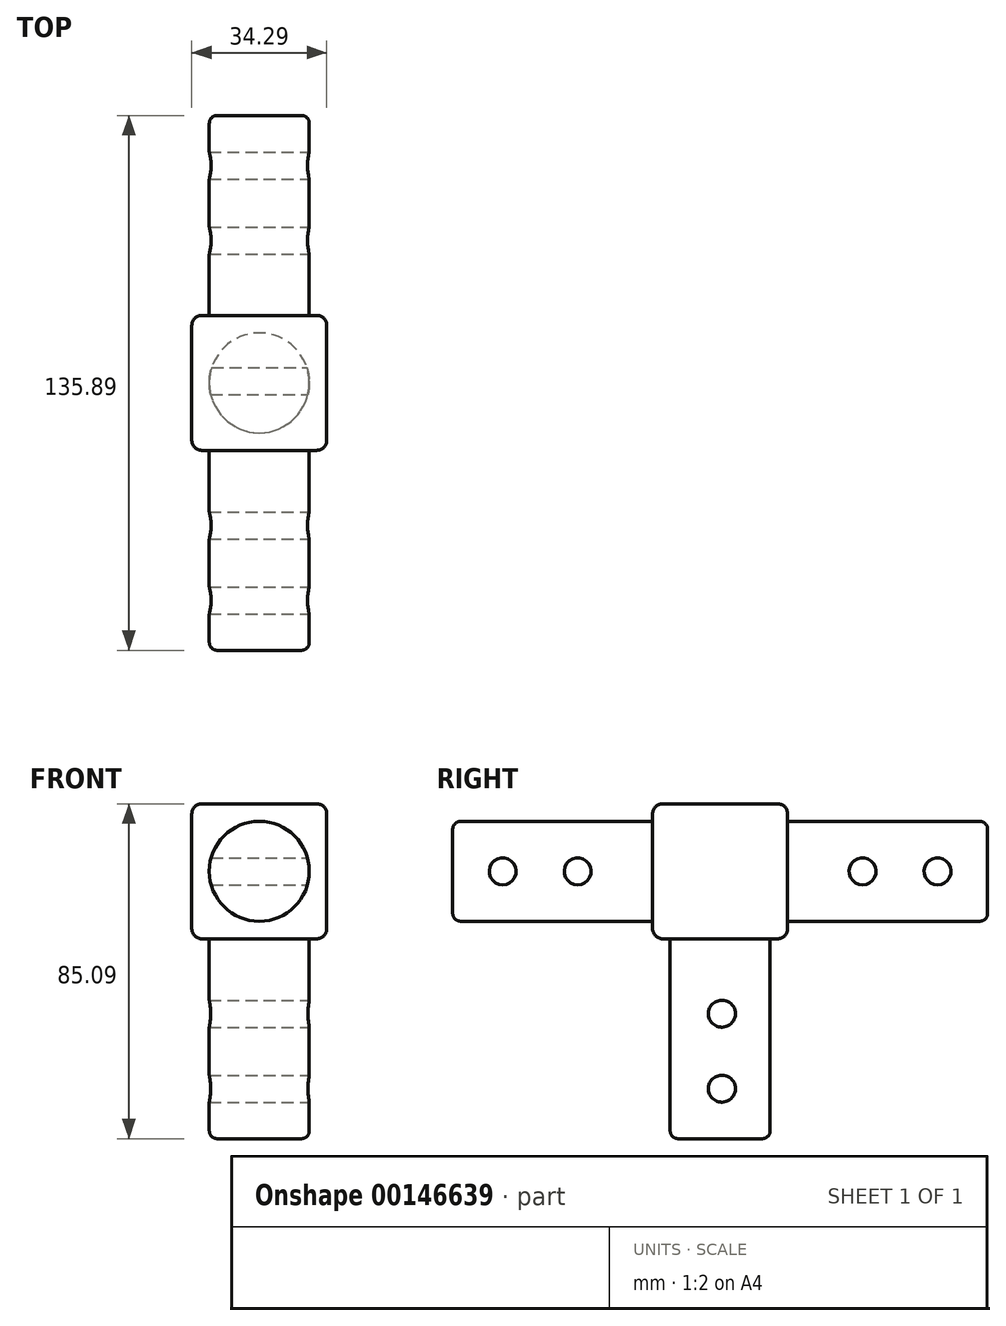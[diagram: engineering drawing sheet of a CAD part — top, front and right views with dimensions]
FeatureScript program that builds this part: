
annotation { "Feature Type Name" : "Feature", "Feature Type Description" : "" }
export const myFeature = defineFeature(function(context is Context, id is Id, definition is map)
    precondition{}
    {
        {
            var Q0;
            Q0=qCreatedBy(makeId("Top.planeOp"),FACE);
            var sketch = newSketch(context, id + "F0", { "sketchPlane" : qUnion([Q0])});
            skLineSegment(sketch, "E0.bottom", {"start": v(-13.47, 23.7) * mm, "end": v(20.82, 23.7) * mm});
            skLineSegment(sketch, "E0.top", {"start": v(-13.47, -10.58) * mm, "end": v(20.82, -10.58) * mm});
            skLineSegment(sketch, "E0.left", {"start": v(-13.47, 23.7) * mm, "end": v(-13.47, -10.58) * mm});
            skLineSegment(sketch, "E0.right", {"start": v(20.82, 23.7) * mm, "end": v(20.82, -10.58) * mm});
            skSolve(sketch);
        }
        {
            var Q0;
            Q0=qSketchRegion(id+"F0",true);
            extrude(context, id + "F1", {"entities" : qUnion([Q0]), "depth" : 34.3 * mm});
        }
        {
            var Q0;
            Q0=makeQuery(id+"F1.opExtrude","SWEPT_FACE",FACE,{"disambiguationData":[OSD([sQuery(id+"F0.wireOp",EDGE,"E0.top")])]});
            var sketch = newSketch(context, id + "F2", { "sketchPlane" : qUnion([Q0])});
            skLineSegment(sketch, "E1", {"start": v(-13.47, 17.15) * mm, "end": v(24.43, 17.15) * mm, "construction": true});
            skLineSegment(sketch, "E2", {"start": v(3.67, 0) * mm, "end": v(3.67, 34.3) * mm, "construction": true});
            skCircle(sketch, "E3", {"center": v(3.67, 17.15) * mm, "radius": 12.7 * mm});
            skSolve(sketch);
        }
        {
            var Q0;
            Q0=qSketchRegion(id+"F2",true);
            extrude(context, id + "F3", {"entities" : qUnion([Q0]), "operationType" : NewBodyOperationType.ADD, "depth" : 50.8 * mm});
        }
        {
            var Q0;
            Q0=qCreatedBy(makeId("Front.planeOp"),FACE);
            var sketch = newSketch(context, id + "F4", { "sketchPlane" : qUnion([Q0])});
            skCircle(sketch, "E4", {"center": v(3.67, 53.34) * mm, "radius": 3.43 * mm});
            skCircle(sketch, "E5", {"center": v(3.67, 72.4) * mm, "radius": 3.43 * mm});
            skSolve(sketch);
        }
        {
            var Q0;
            Q0=qSketchRegion(id+"F4",true);
            extrude(context, id + "F5", {"entities" : qUnion([Q0]), "operationType" : NewBodyOperationType.REMOVE, "endBound" : BoundingType.SYMMETRIC, "oppositeDirection" : true, "depth" : 50.8 * mm});
        }
        {
            var Q0;
            Q0=qCreatedBy(makeId("Right.planeOp"),FACE);
            var sketch = newSketch(context, id + "F6", { "sketchPlane" : qUnion([Q0])});
            skCircle(sketch, "E6", {"center": v(-29.63, 17.15) * mm, "radius": 3.43 * mm});
            skCircle(sketch, "E7", {"center": v(-48.68, 17.15) * mm, "radius": 3.43 * mm});
            skSolve(sketch);
        }
        {
            var Q0;
            Q0=qSketchRegion(id+"F6",true);
            extrude(context, id + "F7", {"entities" : qUnion([Q0]), "operationType" : NewBodyOperationType.REMOVE, "endBound" : BoundingType.SYMMETRIC, "oppositeDirection" : true, "depth" : 50.8 * mm});
        }
        {
            var Q0;
            Q0=qCreatedBy(makeId("Front.planeOp"),FACE);
            var sketch = newSketch(context, id + "F8", { "sketchPlane" : qUnion([Q0])});
            skCircle(sketch, "E8", {"center": v(-51.57, 17.15) * mm, "radius": 3.43 * mm});
            skCircle(sketch, "E9", {"center": v(-32.52, 17.15) * mm, "radius": 3.43 * mm});
            skSolve(sketch);
        }
        {
            var Q0;
            Q0=qSketchRegion(id+"F8",true);
            extrude(context, id + "F9", {"entities" : qUnion([Q0]), "operationType" : NewBodyOperationType.REMOVE, "endBound" : BoundingType.SYMMETRIC, "oppositeDirection" : true, "depth" : 50.8 * mm});
        }
        {
            var Q0;
            Q0=makeQuery(id+"F1.opExtrude","SWEPT_EDGE",EDGE,{"disambiguationData":[OSD([sQuery(id+"F0.wireOp",EDGE,"E0.bottom"),sQuery(id+"F0.wireOp",EDGE,"E0.right")])]});
            var Q1;
            Q1=makeQuery(id+"F1.opExtrude","CAP_EDGE",EDGE,{"disambiguationData":[OSD([sQuery(id+"F0.wireOp",EDGE,"E0.right")])],"isStart":false});
            var Q2;
            Q2=makeQuery(id+"F1.opExtrude","SWEPT_EDGE",EDGE,{"disambiguationData":[OSD([sQuery(id+"F0.wireOp",EDGE,"E0.top"),sQuery(id+"F0.wireOp",EDGE,"E0.right")])]});
            var Q3;
            Q3=makeQuery(id+"F1.opExtrude","CAP_EDGE",EDGE,{"disambiguationData":[OSD([sQuery(id+"F0.wireOp",EDGE,"E0.right")])],"isStart":true});
            var Q4;
            Q4=makeQuery(id+"F1.opExtrude","CAP_EDGE",EDGE,{"disambiguationData":[OSD([sQuery(id+"F0.wireOp",EDGE,"E0.bottom")])],"isStart":true});
            var Q5;
            Q5=makeQuery(id+"F1.opExtrude","CAP_EDGE",EDGE,{"disambiguationData":[OSD([sQuery(id+"F0.wireOp",EDGE,"E0.bottom")])],"isStart":false});
            var Q6;
            Q6=makeQuery(id+"F1.opExtrude","SWEPT_EDGE",EDGE,{"disambiguationData":[OSD([sQuery(id+"F0.wireOp",EDGE,"E0.bottom"),sQuery(id+"F0.wireOp",EDGE,"E0.left")])]});
            var Q7;
            Q7=makeQuery(id+"F1.opExtrude","CAP_EDGE",EDGE,{"disambiguationData":[OSD([sQuery(id+"F0.wireOp",EDGE,"E0.left")])],"isStart":true});
            var Q8;
            Q8=makeQuery(id+"F1.opExtrude","CAP_EDGE",EDGE,{"disambiguationData":[OSD([sQuery(id+"F0.wireOp",EDGE,"E0.top")])],"isStart":true});
            var Q9;
            Q9=makeQuery(id+"F1.opExtrude","CAP_EDGE",EDGE,{"disambiguationData":[OSD([sQuery(id+"F0.wireOp",EDGE,"E0.left")])],"isStart":false});
            var Q10;
            Q10=makeQuery(id+"F1.opExtrude","SWEPT_EDGE",EDGE,{"disambiguationData":[OSD([sQuery(id+"F0.wireOp",EDGE,"E0.top"),sQuery(id+"F0.wireOp",EDGE,"E0.left")])]});
            var Q11;
            Q11=makeQuery(id+"F1.opExtrude","CAP_EDGE",EDGE,{"disambiguationData":[OSD([sQuery(id+"F0.wireOp",EDGE,"E0.top")])],"isStart":false});
            fillet(context, id + "F10", {"entities" : qUnion([Q0, Q1, Q2, Q3, Q4, Q5, Q6, Q7, Q8, Q9, Q10, Q11]), "radius" : 2.54 * mm, "tangentPropagation" : true, "allowEdgeOverflow" : false});
        }
        {
            var Q0;
            Q0=makeQuery(id+"F1.opExtrude","SWEPT_FACE",FACE,{"disambiguationData":[OSD([sQuery(id+"F0.wireOp",EDGE,"E0.bottom")])]});
            var sketch = newSketch(context, id + "F11", { "sketchPlane" : qUnion([Q0])});
            skLineSegment(sketch, "E10", {"start": v(-18.28, 17.15) * mm, "end": v(4.82, 17.15) * mm, "construction": true});
            skPoint(sketch, "E10.endSnap0", {"position": v(-18.28, 17.15) * mm});
            skLineSegment(sketch, "E11", {"start": v(-3.67, 31.75) * mm, "end": v(-3.67, 14.65) * mm, "construction": true});
            skCircle(sketch, "E12", {"center": v(-3.67, 17.15) * mm, "radius": 12.7 * mm});
            skSolve(sketch);
        }
        {
            var Q0;
            Q0=qSketchRegion(id+"F11",true);
            extrude(context, id + "F12", {"entities" : qUnion([Q0]), "operationType" : NewBodyOperationType.ADD, "depth" : 50.8 * mm});
        }
        {
            var Q0;
            Q0=qCreatedBy(makeId("Right.planeOp"),FACE);
            var sketch = newSketch(context, id + "F13", { "sketchPlane" : qUnion([Q0])});
            skCircle(sketch, "E13", {"center": v(42.76, 17.15) * mm, "radius": 3.43 * mm});
            skCircle(sketch, "E14", {"center": v(61.8, 17.15) * mm, "radius": 3.43 * mm});
            skSolve(sketch);
        }
        {
            var Q0;
            Q0=qSketchRegion(id+"F13",true);
            extrude(context, id + "F14", {"entities" : qUnion([Q0]), "operationType" : NewBodyOperationType.REMOVE, "endBound" : BoundingType.SYMMETRIC, "oppositeDirection" : true, "depth" : 50.8 * mm});
        }
        {
            var Q0;
            Q0=qCreatedBy(makeId("Front.planeOp"),FACE);
            var sketch = newSketch(context, id + "F15", { "sketchPlane" : qUnion([Q0])});
            skCircle(sketch, "E15", {"center": v(58.92, 17.15) * mm, "radius": 3.43 * mm});
            skCircle(sketch, "E16", {"center": v(39.87, 17.15) * mm, "radius": 3.43 * mm});
            skSolve(sketch);
        }
        {
            var Q0;
            Q0=qSketchRegion(id+"F15",true);
            extrude(context, id + "F16", {"entities" : qUnion([Q0]), "operationType" : NewBodyOperationType.REMOVE, "endBound" : BoundingType.SYMMETRIC, "oppositeDirection" : true, "depth" : 50.8 * mm});
        }
        {
            var Q0;
            Q0=makeQuery(id+"F1.opExtrude","CAP_FACE",FACE,{"disambiguationData":[OSD([sQuery(id+"F0.wireOp",EDGE,"E0.bottom"),sQuery(id+"F0.wireOp",EDGE,"E0.top"),sQuery(id+"F0.wireOp",EDGE,"E0.left"),sQuery(id+"F0.wireOp",EDGE,"E0.right")])],"isStart":true});
            var sketch = newSketch(context, id + "F17", { "sketchPlane" : qUnion([Q0])});
            skCircle(sketch, "E17", {"center": v(3.67, -6.56) * mm, "radius": 12.7 * mm});
            skPoint(sketch, "E17.centerSnap0", {"position": v(3.67, -21.17) * mm});
            skPoint(sketch, "E17.centerSnap1", {"position": v(18.28, -6.56) * mm});
            skSolve(sketch);
        }
        {
            var Q0;
            Q0=qSketchRegion(id+"F17",true);
            extrude(context, id + "F18", {"entities" : qUnion([Q0]), "operationType" : NewBodyOperationType.ADD, "depth" : 50.8 * mm});
        }
        {
            var Q0;
            Q0=makeQuery(id+"Ff8LsmKBHV4Uzf6_1.opExtrude","CAP_EDGE",EDGE,{"disambiguationData":[OSD([sQuery(id+"FGSIiZxj4pOu3NG_1.wireOp",EDGE,"UelfSfaY-AMup-COUh-hXSA-o5mW5rKARTS6")])],"isStart":false});
            var Q1;
            Q1=makeQuery(id+"F3.opExtrude","CAP_EDGE",EDGE,{"disambiguationData":[OSD([sQuery(id+"F2.wireOp",EDGE,"E3")])],"isStart":false});
            var Q2;
            Q2=makeQuery(id+"FYh3p2H8bsy1Prt_1.opExtrude","CAP_EDGE",EDGE,{"disambiguationData":[OSD([sQuery(id+"FIc3ZwD0MRkNizU_1.wireOp",EDGE,"5X2wenA0-NZPo-tNKO-rhVc-4ux0vwX6K1N9")])],"isStart":false});
            var Q3;
            Q3=makeQuery(id+"F12.opExtrude","CAP_EDGE",EDGE,{"disambiguationData":[OSD([sQuery(id+"F11.wireOp",EDGE,"E12")])],"isStart":false});
            var Q4;
            Q4=makeQuery(id+"F9gDW6ytOR0zG9s_1.opExtrude","CAP_EDGE",EDGE,{"disambiguationData":[OSD([sQuery(id+"FiyRrB6nUQmxvW3_1.wireOp",EDGE,"TDc28uEK-sT7R-I2aJ-wYcu-fXwbEVHNaGzo")])],"isStart":false});
            var Q5;
            Q5=makeQuery(id+"F18.opExtrude","CAP_EDGE",EDGE,{"disambiguationData":[OSD([sQuery(id+"F17.wireOp",EDGE,"E17")])],"isStart":false});
            fillet(context, id + "F19", {"entities" : qUnion([Q0, Q1, Q2, Q3, Q4, Q5]), "radius" : 2.03 * mm, "tangentPropagation" : true, "allowEdgeOverflow" : false});
        }
        {
            var Q0;
            Q0=qCreatedBy(makeId("Right.planeOp"),FACE);
            var sketch = newSketch(context, id + "F20", { "sketchPlane" : qUnion([Q0])});
            skCircle(sketch, "E18", {"center": v(7.01, -19.05) * mm, "radius": 3.43 * mm});
            skCircle(sketch, "E19", {"center": v(7.01, -38.1) * mm, "radius": 3.43 * mm});
            skSolve(sketch);
        }
        {
            var Q0;
            Q0=qSketchRegion(id+"F20",true);
            extrude(context, id + "F21", {"entities" : qUnion([Q0]), "operationType" : NewBodyOperationType.REMOVE, "endBound" : BoundingType.SYMMETRIC, "oppositeDirection" : true, "depth" : 50.8 * mm});
        }
    });
